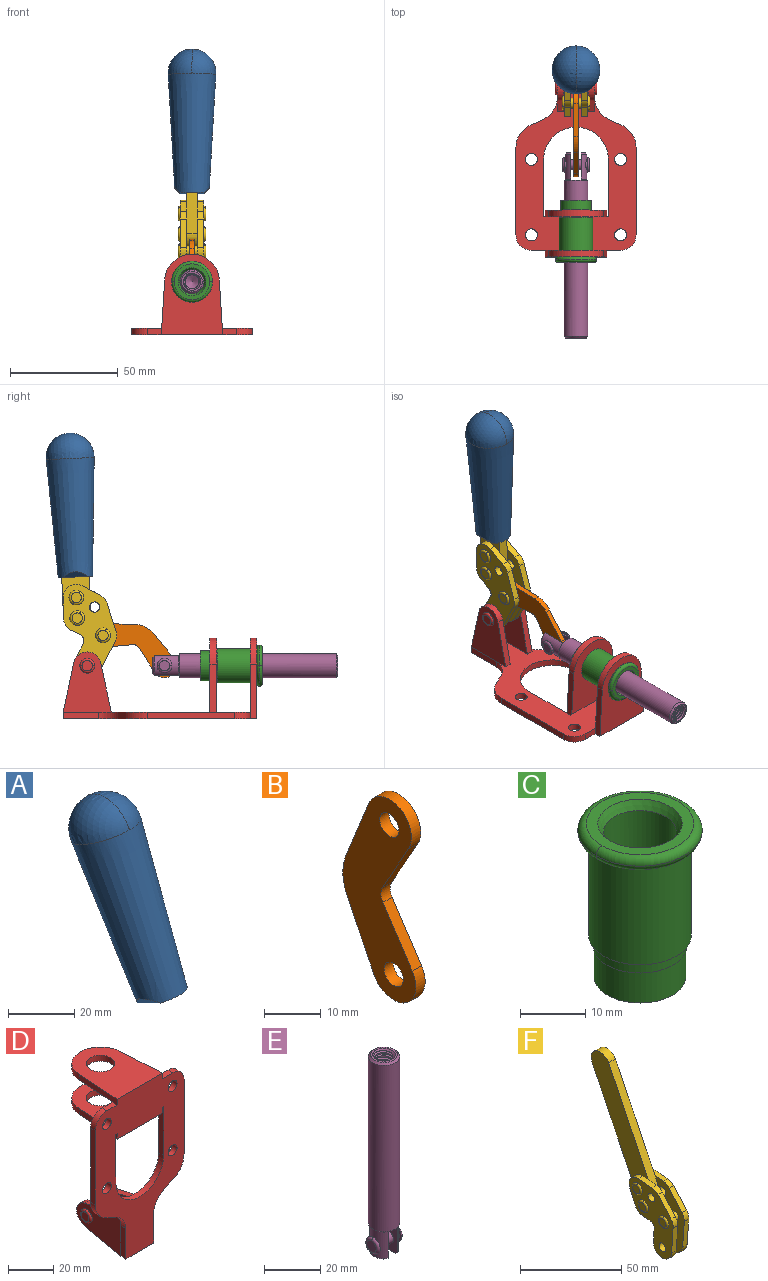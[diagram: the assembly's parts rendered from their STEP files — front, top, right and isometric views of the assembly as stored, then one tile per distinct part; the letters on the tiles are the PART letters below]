
ASSEMBLY  parts=6 mates=6
PART A: 11 faces, bbox 22.3x42.6x64.5 mm
  f0: sphere r=11.13mm, area 411.4mm2, adj f1,f8
  f1: cone r=11.11mm half-angle=3.3deg, axis (0,0.44,0.9), area 3251.8mm2, adj f0,f7,f8,f9,f10
  f2: cylinder r=6.16mm len=11.7mm, axis (1,0,0), area 89.5mm2, adj f3,f4,f5,f6
  f3: plane 60.23x36.75mm, normal (-1,0,0), area 763.6mm2, adj f2,f4,f6,f10
  f4: plane 51.37x25.05mm, normal (0,0.9,-0.44), area 264.2mm2, adj f2,f3,f5,f10
  f5: plane 60.23x36.75mm, normal (1,0,0), area 763.6mm2, adj f2,f4,f6,f10
  f6: plane 51.37x25.05mm, normal (0,-0.9,0.44), area 264.2mm2, adj f2,f3,f5,f10
  f7: plane 9.95x5.95mm, normal (0.71,-0.31,-0.64), area 25.8mm2, adj f1,f10
  f8: sphere r=11.13mm, area 411.4mm2, adj f0,f1
  f9: plane 9.95x5.95mm, normal (-0.71,-0.31,-0.64), area 25.8mm2, adj f1,f10
  f10: plane 14.27x11.38mm, normal (0,-0.44,-0.9), area 106.7mm2, adj f1,f3,f4,f5,f6,f7,f9
PART B: 12 faces, bbox 2.3x18.2x42.8 mm
  f0: cylinder r=2.4mm len=4.8mm, axis (1,0,0), area 34.9mm2, adj f4,f11
  f1: cylinder r=10.41mm len=8.47mm, axis (1,0,0), area 20.2mm2, adj f4,f9,f10,f11
  f2: cylinder r=3.05mm len=3.16mm, axis (1,0,0), area 7.7mm2, adj f4,f6,f7,f11
  f3: cylinder r=2.4mm len=4.8mm, axis (1,0,0), area 34.9mm2, adj f4,f11
  f4: plane 42.81x18.23mm, normal (-1,0,0), area 414.1mm2, adj f0,f1,f2,f3,f5,f6,f7,f8
  f5: cylinder r=5.54mm len=10.67mm, axis (1,0,0), area 41.8mm2, adj f4,f6,f10,f11
  f6: plane 11.66x6.53mm, normal (0,-0.87,-0.49), area 30.9mm2, adj f2,f4,f5,f11
  f7: plane 11.17x7.33mm, normal (0,-0.84,0.55), area 30.9mm2, adj f2,f4,f8,f11
  f8: cylinder r=5.54mm len=10.51mm, axis (1,0,0), area 41.8mm2, adj f4,f7,f9,f11
  f9: plane 13.67x6.67mm, normal (0,0.9,-0.44), area 35.1mm2, adj f1,f4,f8,f11
  f10: plane 14.1x5.7mm, normal (0,0.93,0.37), area 35.1mm2, adj f1,f4,f5,f11
  f11: plane 42.81x18.23mm, normal (1,0,0), area 414.1mm2, adj f0,f1,f2,f3,f5,f6,f7,f8
PART C: 15 faces, bbox 20.6x20.6x28.7 mm
  f0: torus R=8.26mm, axis (0,0,1), area 56.8mm2, adj f1,f10,f12
  f1: torus R=8.26mm, axis (0,0,1), area 56.8mm2, adj f0,f6,f13
  f2: cylinder r=5.59mm len=25.91mm, axis (0,0,1), area 909.6mm2, adj f3,f4
  f3: cone r=6.86mm half-angle=45deg, axis (0,0,-1), area 70.2mm2, adj f2,f14
  f4: cone r=6.47mm half-angle=30deg, axis (0,0,1), area 66.7mm2, adj f2,f13
  f5: cylinder r=7.04mm len=14.07mm, axis (0,0,1), area 252.6mm2, adj f11,f14
  f6: torus R=8.26mm, axis (0,0,1), area 56.8mm2, adj f1,f12,f13
  f7: cylinder r=7.16mm len=14.33mm, axis (0,0,1), area 91.5mm2, adj f9,f11
  f8: cylinder r=7.86mm len=18.42mm, axis (0,0,1), area 909.6mm2, adj f9,f10
  f9: plane 15.72x15.72mm, normal (0,0,-1), area 33mm2, adj f7,f8
  f10: plane 16.51x16.51mm, normal (0,0,-1), area 19.9mm2, adj f0,f8,f12
  f11: plane 14.33x14.33mm, normal (0,0,-1), area 5.7mm2, adj f5,f7
  f12: torus R=8.26mm, axis (0,0,1), area 56.8mm2, adj f0,f6,f10
  f13: plane 16.51x16.51mm, normal (0,0,1), area 82.7mm2, adj f1,f4,f6
  f14: plane 14.07x14.07mm, normal (0,0,-1), area 7.8mm2, adj f3,f5
PART D: 55 faces, bbox 55.7x37.4x89.8 mm
  f0: torus R=2.41mm, axis (-1,0,0), area 15mm2, adj f11,f15,f25
  f1: torus R=2.41mm, axis (-1,0,0), area 15mm2, adj f10,f12,f22
  f2: cylinder r=2.78mm len=5.56mm, axis (0,-1,0), area 54.2mm2, adj f30,f54
  f3: cylinder r=14.99mm len=29.97mm, axis (0,-1,0), area 145.9mm2, adj f30,f49,f53,f54
  f4: cylinder r=2.78mm len=5.56mm, axis (0,-1,0), area 54.2mm2, adj f30,f54
  f5: cylinder r=2.78mm len=5.56mm, axis (0,-1,0), area 54.2mm2, adj f30,f54
  f6: cylinder r=2.78mm len=5.56mm, axis (0,-1,0), area 54.2mm2, adj f30,f54
  f7: cylinder r=6.35mm len=12.7mm, axis (0,0,1), area 123.6mm2, adj f27,f51
  f8: cylinder r=6.35mm len=12.7mm, axis (0,0,-1), area 124.7mm2, adj f21,f35
  f9: cylinder r=2.41mm len=11.18mm, axis (-1,0,0), area 169.4mm2, adj f16,f19
  f10: plane 4.83x4.83mm, normal (1,0,0), area 18.3mm2, adj f1,f12
  f11: plane 4.83x4.83mm, normal (-1,0,0), area 18.3mm2, adj f0,f15
  f12: torus R=2.41mm, axis (-1,0,0), area 15mm2, adj f1,f10,f22
  f13: cylinder r=6.35mm len=12.41mm, axis (1,0,0), area 53.4mm2, adj f18,f19,f22,f23
  f14: cylinder r=6.35mm len=12.41mm, axis (-1,0,0), area 53.4mm2, adj f16,f17,f24,f25
  f15: torus R=2.41mm, axis (-1,0,0), area 15mm2, adj f0,f11,f25
  f16: plane 27.86x22.35mm, normal (1,0,0), area 425.4mm2, adj f9,f14,f17,f24,f30
  f17: plane 22.86x4.97mm, normal (0,0.21,0.98), area 72.5mm2, adj f14,f16,f25,f30
  f18: plane 22.86x4.97mm, normal (0,0.21,0.98), area 72.5mm2, adj f13,f19,f22,f30
  f19: plane 27.86x22.35mm, normal (-1,0,0), area 425.4mm2, adj f9,f13,f18,f23,f30
  f20: cylinder r=12.7mm len=25.35mm, axis (0,0,-1), area 119.8mm2, adj f21,f34,f35,f36
  f21: plane 34.21x28.07mm, normal (0,0,-1), area 702.4mm2, adj f8,f20,f30,f34,f36
  f22: plane 27.96x22.45mm, normal (1,0,0), area 407.2mm2, adj f1,f12,f13,f18,f23,f30,f42,f43
  f23: plane 22.86x4.97mm, normal (0,0.21,-0.98), area 72.5mm2, adj f13,f19,f22,f44
  f24: plane 22.86x4.97mm, normal (0,0.21,-0.98), area 72.5mm2, adj f14,f16,f25,f44
  f25: plane 27.86x22.35mm, normal (-1,0,0), area 407.1mm2, adj f0,f14,f15,f17,f24,f30,f45,f46
  f26: plane 3.1x0.95mm, normal (0,0,-1), area 2.7mm2, adj f30,f49,f50,f54
  f27: plane 34.21x28.07mm, normal (0,0,1), area 702.4mm2, adj f7,f28,f30,f50,f52
  f28: cylinder r=12.7mm len=25.35mm, axis (0,0,1), area 118.8mm2, adj f27,f50,f51,f52
  f29: plane 3.1x0.95mm, normal (0,0,-1), area 2.7mm2, adj f30,f52,f53,f54
  f30: plane 86.54x55.63mm, normal (0,1,0), area 2362.9mm2, adj f2,f3,f4,f5,f6,f16,f17,f18
  f31: plane 40.56x3.1mm, normal (-1,0,0), area 125.7mm2, adj f30,f32,f48,f54
  f32: cylinder r=7.11mm len=7.11mm, axis (0,-1,0), area 34.6mm2, adj f30,f31,f33,f54
  f33: plane 6.67x3.1mm, normal (0,0,1), area 20.4mm2, adj f30,f32,f34,f54
  f34: plane 25.39x3.13mm, normal (-1,0.06,0), area 79.5mm2, adj f20,f21,f33,f35,f54
  f35: plane 37.31x28.45mm, normal (0,0,1), area 789.9mm2, adj f8,f20,f34,f36,f54
  f36: plane 25.39x3.13mm, normal (1,0.06,0), area 79.5mm2, adj f20,f21,f35,f37,f54
  f37: plane 6.67x3.1mm, normal (0,0,1), area 20.4mm2, adj f30,f36,f38,f54
  f38: cylinder r=7.11mm len=7.11mm, axis (0,-1,0), area 34.6mm2, adj f30,f37,f39,f54
  f39: plane 40.56x3.1mm, normal (1,0,0), area 125.7mm2, adj f30,f38,f40,f54
  f40: cylinder r=11.18mm len=10.16mm, axis (0,-1,0), area 39.5mm2, adj f30,f39,f41,f54
  f41: plane 6.09x3.1mm, normal (0.42,0,-0.91), area 20.8mm2, adj f30,f40,f42,f54
  f42: cylinder r=11.18mm len=9.41mm, axis (0,-1,0), area 37.2mm2, adj f22,f30,f41,f43,f54
  f43: plane 16.5x3.1mm, normal (1,0,0), area 51.1mm2, adj f22,f42,f44,f54
  f44: plane 17.37x3.1mm, normal (0,0,-1), area 53.8mm2, adj f23,f24,f30,f43,f45,f54
  f45: plane 16.5x3.1mm, normal (-1,0,0), area 51.1mm2, adj f25,f44,f46,f54
  f46: cylinder r=11.18mm len=9.41mm, axis (0,-1,0), area 37.2mm2, adj f25,f30,f45,f47,f54
  f47: plane 6.09x3.1mm, normal (-0.42,0,-0.91), area 20.8mm2, adj f30,f46,f48,f54
  f48: cylinder r=11.18mm len=10.16mm, axis (0,-1,0), area 39.5mm2, adj f30,f31,f47,f54
  f49: plane 26.54x3.1mm, normal (-1,0,0), area 82.3mm2, adj f3,f26,f30,f54
  f50: plane 25.39x3.1mm, normal (1,0.06,0), area 78.8mm2, adj f26,f27,f28,f51,f54
  f51: plane 37.31x28.45mm, normal (0,0,-1), area 789.9mm2, adj f7,f28,f50,f52,f54
  f52: plane 25.39x3.1mm, normal (-1,0.06,0), area 78.8mm2, adj f27,f28,f29,f51,f54
  f53: plane 26.54x3.1mm, normal (1,0,0), area 82.3mm2, adj f3,f29,f30,f54
  f54: plane 89.66x55.63mm, normal (0,-1,0), area 2678.5mm2, adj f2,f3,f4,f5,f6,f26,f29,f31
PART E: 48 faces, bbox 12.6x11.1x86.1 mm
  f0: torus R=2.41mm, axis (-1,0,0), area 15mm2, adj f30,f32,f34
  f1: torus R=2.41mm, axis (-1,0,0), area 15mm2, adj f29,f31,f33
  f2: cylinder r=5.54mm len=72.39mm, axis (0,0,1), area 2518.5mm2, adj f3,f4,f42,f43
  f3: cone r=5.54mm half-angle=45deg, axis (0,0,1), area 7.6mm2, adj f2,f5,f41
  f4: cone r=5.54mm half-angle=45deg, axis (0,0,-1), area 34.9mm2, adj f2,f39
  f5: cylinder r=5.08mm len=11.48mm, axis (0,0,1), area 108.3mm2, adj f3,f7,f8,f41
  f6: cylinder r=2.41mm len=4.83mm, axis (-1,0,0), area 71.2mm2, adj f40,f41
  f7: cylinder r=2.41mm len=4.83mm, axis (-1,0,0), area 7.6mm2, adj f5,f34
  f8: cone r=5.08mm half-angle=45deg, axis (0,0,1), area 10.6mm2, adj f5,f37,f41
  f9: cone r=3.98mm half-angle=45deg, axis (0,0,1), area 17.6mm2, adj f27,f39,f45,f46,f47
  f10: cylinder r=2.41mm len=4.83mm, axis (-1,0,0), area 7.6mm2, adj f33,f38
  f11: cylinder r=3.2mm len=6.4mm, axis (0,0,1), area 78.4mm2, adj f12,f28,f44,f45,f47
  f12: cylinder r=3.2mm len=6.4mm, axis (0,0,1), area 10.5mm2, adj f11,f13,f45,f47
  f13: cylinder r=3.2mm len=6.4mm, axis (0,0,1), area 10.5mm2, adj f12,f14,f45,f47
  f14: cylinder r=3.2mm len=6.4mm, axis (0,0,1), area 10.5mm2, adj f13,f15,f45,f47
  f15: cylinder r=3.2mm len=6.4mm, axis (0,0,1), area 10.5mm2, adj f14,f16,f45,f47
  f16: cylinder r=3.2mm len=6.4mm, axis (0,0,1), area 10.5mm2, adj f15,f17,f45,f47
  f17: cylinder r=3.2mm len=6.4mm, axis (0,0,1), area 10.5mm2, adj f16,f18,f45,f47
  f18: cylinder r=3.2mm len=6.4mm, axis (0,0,1), area 10.5mm2, adj f17,f19,f45,f47
  f19: cylinder r=3.2mm len=6.4mm, axis (0,0,1), area 10.5mm2, adj f18,f20,f45,f47
  f20: cylinder r=3.2mm len=6.4mm, axis (0,0,1), area 10.5mm2, adj f19,f21,f45,f47
  f21: cylinder r=3.2mm len=6.4mm, axis (0,0,1), area 10.5mm2, adj f20,f22,f45,f47
  f22: cylinder r=3.2mm len=6.4mm, axis (0,0,1), area 10.5mm2, adj f21,f23,f45,f47
  f23: cylinder r=3.2mm len=6.4mm, axis (0,0,1), area 10.5mm2, adj f22,f24,f45,f47
  f24: cylinder r=3.2mm len=6.4mm, axis (0,0,1), area 10.5mm2, adj f23,f25,f45,f47
  f25: cylinder r=3.2mm len=6.4mm, axis (0,0,1), area 10.5mm2, adj f24,f26,f45,f47
  f26: cylinder r=3.2mm len=6.4mm, axis (0,0,1), area 10.5mm2, adj f25,f27,f45,f47
  f27: cylinder r=3.2mm len=6.4mm, axis (0,0,1), area 7.4mm2, adj f9,f26,f45,f47
  f28: cone r=3.2mm half-angle=60deg, axis (0,0,1), area 37.2mm2, adj f11
  f29: plane 4.83x4.83mm, normal (-1,0,0), area 18.3mm2, adj f1,f31
  f30: plane 4.83x4.83mm, normal (1,0,0), area 18.3mm2, adj f0,f32
  f31: torus R=2.41mm, axis (-1,0,0), area 15mm2, adj f1,f29,f33
  f32: torus R=2.41mm, axis (-1,0,0), area 15mm2, adj f0,f30,f34
  f33: plane 6.83x6.83mm, normal (1,0,0), area 18.3mm2, adj f1,f10,f31
  f34: plane 6.83x6.83mm, normal (-1,0,0), area 18.3mm2, adj f0,f7,f32
  f35: cone r=5.08mm half-angle=45deg, axis (0,0,1), area 10.6mm2, adj f36,f38,f40
  f36: plane 7.25x1.97mm, normal (0,0,-1), area 10mm2, adj f35,f40
  f37: plane 7.25x1.97mm, normal (0,0,-1), area 10mm2, adj f8,f41
  f38: cylinder r=5.08mm len=11.48mm, axis (0,0,1), area 108.3mm2, adj f10,f35,f40,f42
  f39: plane 9.55x9.55mm, normal (0,0,1), area 22mm2, adj f4,f9
  f40: plane 12.76x10.09mm, normal (1,0,0), area 95.7mm2, adj f6,f35,f36,f38,f42,f43
  f41: plane 12.76x10.09mm, normal (-1,0,0), area 95.7mm2, adj f3,f5,f6,f8,f37,f43
  f42: cone r=5.54mm half-angle=45deg, axis (0,0,1), area 7.6mm2, adj f2,f38,f40
  f43: plane 11.07x4.7mm, normal (0,0,-1), area 50.4mm2, adj f2,f40,f41
  f44: plane 0.89x0.62mm, normal (-1,0,0), area 0.3mm2, adj f11,f45,f46,f47
  f45: bspline ~24.8x7.63mm, area 266.6mm2, adj f9,f11,f12,f13,f14,f15,f16,f17
  f46: bspline ~24.87x7.63mm, area 73.6mm2, adj f9,f44,f45,f47
  f47: bspline ~24.98x7.63mm, area 272.5mm2, adj f9,f11,f12,f13,f14,f15,f16,f17
PART F: 59 faces, bbox 12.9x60.2x99.6 mm
  f0: torus R=2.39mm, axis (-1,0,0), area 14.9mm2, adj f20,f43,f51
  f1: torus R=2.39mm, axis (-1,0,0), area 14.9mm2, adj f19,f42,f51
  f2: torus R=2.39mm, axis (-1,0,0), area 14.9mm2, adj f18,f35,f51
  f3: torus R=2.39mm, axis (-1,0,0), area 14.9mm2, adj f14,f17,f23
  f4: torus R=2.39mm, axis (-1,0,0), area 14.9mm2, adj f13,f16,f23
  f5: torus R=2.39mm, axis (-1,0,0), area 14.9mm2, adj f12,f15,f23
  f6: cylinder r=2.39mm len=4.78mm, axis (1,0,0), area 46.5mm2, adj f48,f50,f51
  f7: cylinder r=2.39mm len=4.78mm, axis (1,0,0), area 46.5mm2, adj f50,f51
  f8: cylinder r=6.35mm len=12.68mm, axis (1,0,0), area 61.8mm2, adj f38,f39,f50,f51
  f9: cylinder r=2.39mm len=4.78mm, axis (-1,0,0), area 70.5mm2, adj f46,f50
  f10: cylinder r=2.39mm len=4.78mm, axis (-1,0,0), area 46.5mm2, adj f23,f45,f46
  f11: cylinder r=2.39mm len=4.78mm, axis (-1,0,0), area 46.5mm2, adj f23,f46
  f12: plane 4.78x4.78mm, normal (1,0,0), area 17.9mm2, adj f5,f15
  f13: plane 4.78x4.78mm, normal (1,0,0), area 17.9mm2, adj f4,f16
  f14: plane 4.78x4.78mm, normal (1,0,0), area 17.9mm2, adj f3,f17
  f15: torus R=2.39mm, axis (-1,0,0), area 14.9mm2, adj f5,f12,f23
  f16: torus R=2.39mm, axis (-1,0,0), area 14.9mm2, adj f4,f13,f23
  f17: torus R=2.39mm, axis (-1,0,0), area 14.9mm2, adj f3,f14,f23
  f18: plane 4.78x4.78mm, normal (-1,0,0), area 17.9mm2, adj f2,f35
  f19: plane 4.78x4.78mm, normal (-1,0,0), area 17.9mm2, adj f1,f42
  f20: plane 4.78x4.78mm, normal (-1,0,0), area 17.9mm2, adj f0,f43
  f21: plane 2.26x0.2mm, normal (1,0,0), area 0.2mm2, adj f31,f44
  f22: plane 2.26x0.2mm, normal (-1,0,0), area 0.2mm2, adj f41,f44
  f23: plane 39.37x30.77mm, normal (1,0,0), area 565.5mm2, adj f3,f4,f5,f10,f11,f15,f16,f17
  f24: cylinder r=6.1mm len=4.15mm, axis (-1,0,0), area 14.7mm2, adj f23,f25,f32,f46
  f25: plane 10.25x9.01mm, normal (0,-0.75,0.66), area 42.3mm2, adj f23,f24,f26,f46
  f26: cylinder r=6.35mm len=4.64mm, axis (-1,0,0), area 15.6mm2, adj f23,f25,f27,f46
  f27: plane 15.84x3.1mm, normal (0,-1,-0.07), area 49.2mm2, adj f23,f26,f28,f46
  f28: cylinder r=6.35mm len=12.68mm, axis (-1,0,0), area 61.8mm2, adj f23,f27,f29,f46
  f29: plane 8.11x3.1mm, normal (0,1,0.07), area 25.2mm2, adj f23,f28,f30,f46
  f30: cylinder r=3.05mm len=3.25mm, axis (-1,0,0), area 14.8mm2, adj f23,f29,f31,f46
  f31: plane 5.99x3.1mm, normal (0,0.07,-1), area 18.6mm2, adj f21,f23,f30,f44,f46
  f32: plane 9.5x3.1mm, normal (0,-0.07,1), area 29.5mm2, adj f23,f24,f33,f46,f47
  f33: cylinder r=6.1mm len=8.63mm, axis (-1,0,0), area 39.1mm2, adj f23,f32,f34,f47
  f34: plane 8.65x3.96mm, normal (0,0.91,-0.42), area 29.5mm2, adj f23,f33,f44,f47
  f35: torus R=2.39mm, axis (-1,0,0), area 14.9mm2, adj f2,f18,f51
  f36: plane 10.25x9.01mm, normal (0,-0.75,0.66), area 42.3mm2, adj f37,f49,f50,f51
  f37: cylinder r=6.35mm len=4.64mm, axis (1,0,0), area 15.6mm2, adj f36,f38,f50,f51
  f38: plane 15.84x3.1mm, normal (0,-1,-0.07), area 49.2mm2, adj f8,f37,f50,f51
  f39: plane 8.11x3.1mm, normal (0,1,0.07), area 25.2mm2, adj f8,f40,f50,f51
  f40: cylinder r=3.05mm len=3.25mm, axis (1,0,0), area 14.8mm2, adj f39,f41,f50,f51
  f41: plane 5.99x3.1mm, normal (0,0.07,-1), area 18.6mm2, adj f22,f40,f44,f50,f51
  f42: torus R=2.39mm, axis (-1,0,0), area 14.9mm2, adj f1,f19,f51
  f43: torus R=2.39mm, axis (-1,0,0), area 14.9mm2, adj f0,f20,f51
  f44: cylinder r=6.35mm len=12.12mm, axis (-1,0,0), area 128.9mm2, adj f21,f22,f23,f31,f34,f41,f46,f47
  f45: plane 2.65x1.35mm, normal (1,0,0), area 1mm2, adj f10,f55
  f46: plane 39.08x20.42mm, normal (-1,0,0), area 412.5mm2, adj f9,f10,f11,f24,f25,f26,f27,f28
  f47: plane 77.62x39.82mm, normal (1,0,0), area 850mm2, adj f32,f33,f34,f44,f53,f54,f55
  f48: plane 2.65x1.35mm, normal (-1,0,0), area 1mm2, adj f6,f55
  f49: cylinder r=6.1mm len=4.15mm, axis (1,0,0), area 14.7mm2, adj f36,f50,f51,f56
  f50: plane 39.08x20.42mm, normal (1,0,0), area 412.5mm2, adj f6,f7,f8,f9,f36,f37,f38,f39
  f51: plane 39.37x30.77mm, normal (-1,0,0), area 565.5mm2, adj f0,f1,f2,f6,f7,f8,f35,f36
  f52: plane 8.65x3.96mm, normal (0,0.91,-0.42), area 29.5mm2, adj f44,f51,f57,f58
  f53: plane 68.49x33.4mm, normal (0,0.9,-0.44), area 358.1mm2, adj f44,f47,f54,f58
  f54: cylinder r=6.35mm len=12.06mm, axis (1,0,0), area 93.7mm2, adj f47,f53,f55,f58
  f55: plane 68.49x33.4mm, normal (0,-0.9,0.44), area 358.1mm2, adj f44,f45,f46,f47,f48,f50,f54,f58
  f56: plane 9.5x3.1mm, normal (0,-0.07,1), area 29.5mm2, adj f49,f50,f51,f57,f58
  f57: cylinder r=6.1mm len=8.63mm, axis (1,0,0), area 39.1mm2, adj f51,f52,f56,f58
  f58: plane 77.62x39.82mm, normal (-1,0,0), area 850mm2, adj f44,f52,f53,f54,f55,f56,f57
PLACE A rot(axis=(1,0,0),23.5deg) t=(0,6.05,41.15)mm
PLACE B rot(axis=(1,0,0),118.3deg) t=(0,30.93,7.2)mm
PLACE C rot(axis=(1,0,0),90deg) t=(0,9.31,-3.1)mm
PLACE D rot(axis=(1,0,0),90deg) t=(0,9.31,-3.1)mm fixed
PLACE E rot(axis=(1,0,0),90deg) t=(0,21.1,-3.1)mm
PLACE F rot(axis=(1,0,0),23.5deg) t=(0,6.05,41.15)mm
MATE fastened C.f2 <-> D.f7  axis (0,1,0) through (0,-37.09,21.51)mm
MATE revolute B.f5 <-> E.f6  axis (1,0,0) through (0,5.62,21.51)mm
MATE fastened F.f54 <-> A.f2  axis (1,0,0) through (0,49.4,119.68)mm
MATE revolute B.f3 <-> F.f4  axis (1,0,0) through (0,34.08,35.6)mm
MATE revolute F.f7 <-> D.f0  axis (-1,0,0) through (0,41.4,21.51)mm
MATE slider E.f2 <-> D.f7  axis (0,-1,0) through (0,-37.68,21.51)mm
